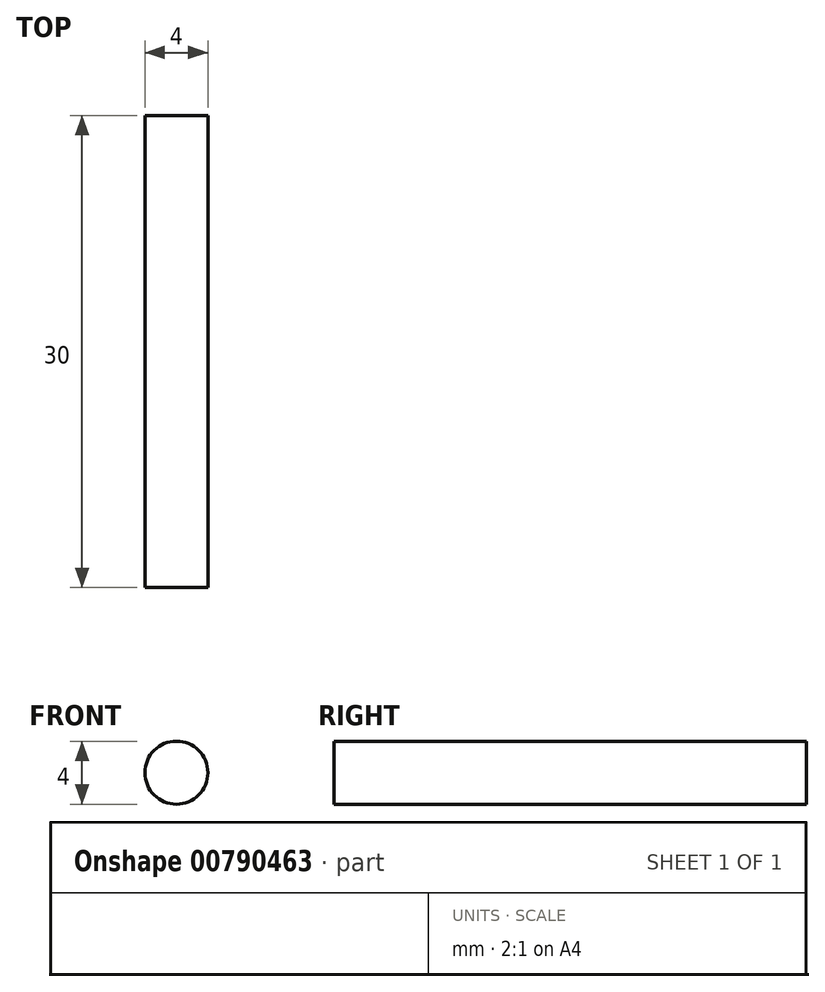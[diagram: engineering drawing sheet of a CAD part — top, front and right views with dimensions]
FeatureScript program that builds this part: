
annotation { "Feature Type Name" : "Feature", "Feature Type Description" : "" }
export const myFeature = defineFeature(function(context is Context, id is Id, definition is map)
    precondition{}
    {
        {
            var Q0;
            Q0=qCreatedBy(makeId("Front.planeOp"),FACE);
            var sketch = newSketch(context, id + "F0", { "sketchPlane" : qUnion([Q0])});
            skCircle(sketch, "E0", {"center": v(0, 0) * mm, "radius": 2 * mm});
            skSolve(sketch);
        }
        {
            var Q0;
            Q0 = qSketchRegion(id + "F0", true);
            extrude(context, id + "F1", {"entities" : qUnion([Q0]), "depth" : 30 * mm, "offsetDistance" : 25 * mm});
        }
    });
